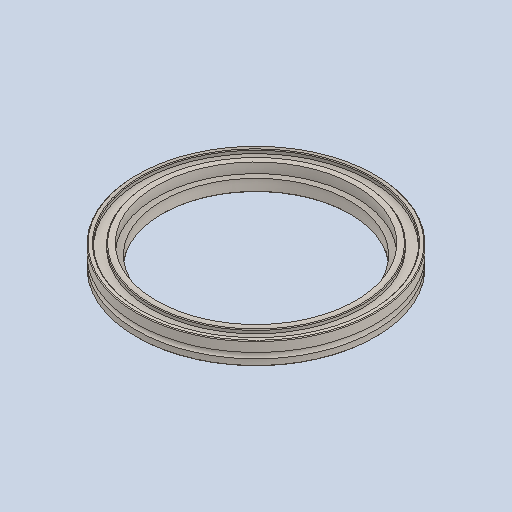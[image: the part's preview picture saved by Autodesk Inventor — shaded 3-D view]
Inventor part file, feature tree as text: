
AUTODESK INVENTOR PART (.ipt)
format: ipt  version: 2023 (Build 270158000, 158)  size: 162,816 bytes
history: native  units: in
note: dims shown in document units (in); Inventor stores cm internally (conversion verified against a paired STEP export)
features: extrude x1
ambient origin geometry x8: Origin, YZ Plane, XZ Plane, XY Plane, X Axis, Y Axis, Z Axis, Center Point
bodies: Solid1 (feature_tree)
feature tree (1):
  extrude  "Extrude2"  [1 undecoded]
note: 1 required parameter value undecoded (feature->parameter linkage not recoverable at this tier; creation-order binding heuristic only, values carry confidence <= 0.55)
